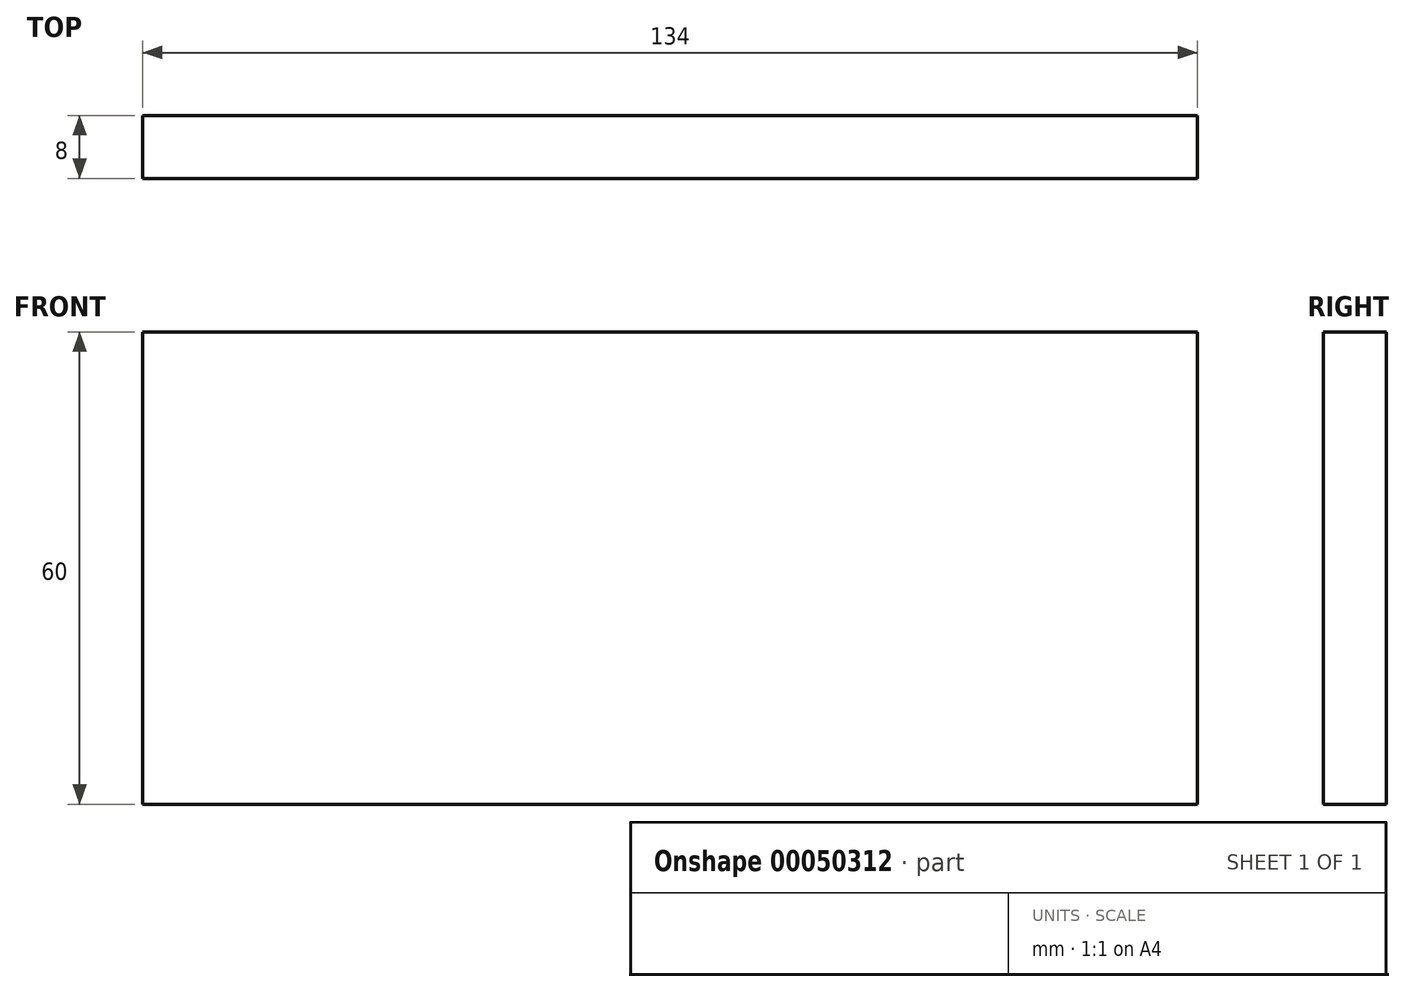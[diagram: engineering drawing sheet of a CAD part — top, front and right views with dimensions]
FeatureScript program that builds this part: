
annotation { "Feature Type Name" : "Feature", "Feature Type Description" : "" }
export const myFeature = defineFeature(function(context is Context, id is Id, definition is map)
    precondition{}
    {
        {
            var Q0;
            Q0=qCreatedBy(makeId("Front.planeOp"),FACE);
            var sketch = newSketch(context, id + "F0", { "sketchPlane" : qUnion([Q0])});
            skLineSegment(sketch, "E0.bottom", {"start": v(0, 0) * mm, "end": v(-134, 0) * mm});
            skLineSegment(sketch, "E0.top", {"start": v(0, -60) * mm, "end": v(-134, -60) * mm});
            skLineSegment(sketch, "E0.left", {"start": v(0, 0) * mm, "end": v(0, -60) * mm});
            skLineSegment(sketch, "E0.right", {"start": v(-134, 0) * mm, "end": v(-134, -60) * mm});
            skSolve(sketch);
        }
        {
            var Q0;
            Q0 = qSketchRegion(id + "F0", true);
            extrude(context, id + "F1", {"entities" : qUnion([Q0]), "depth" : 8 * mm});
        }
    });
